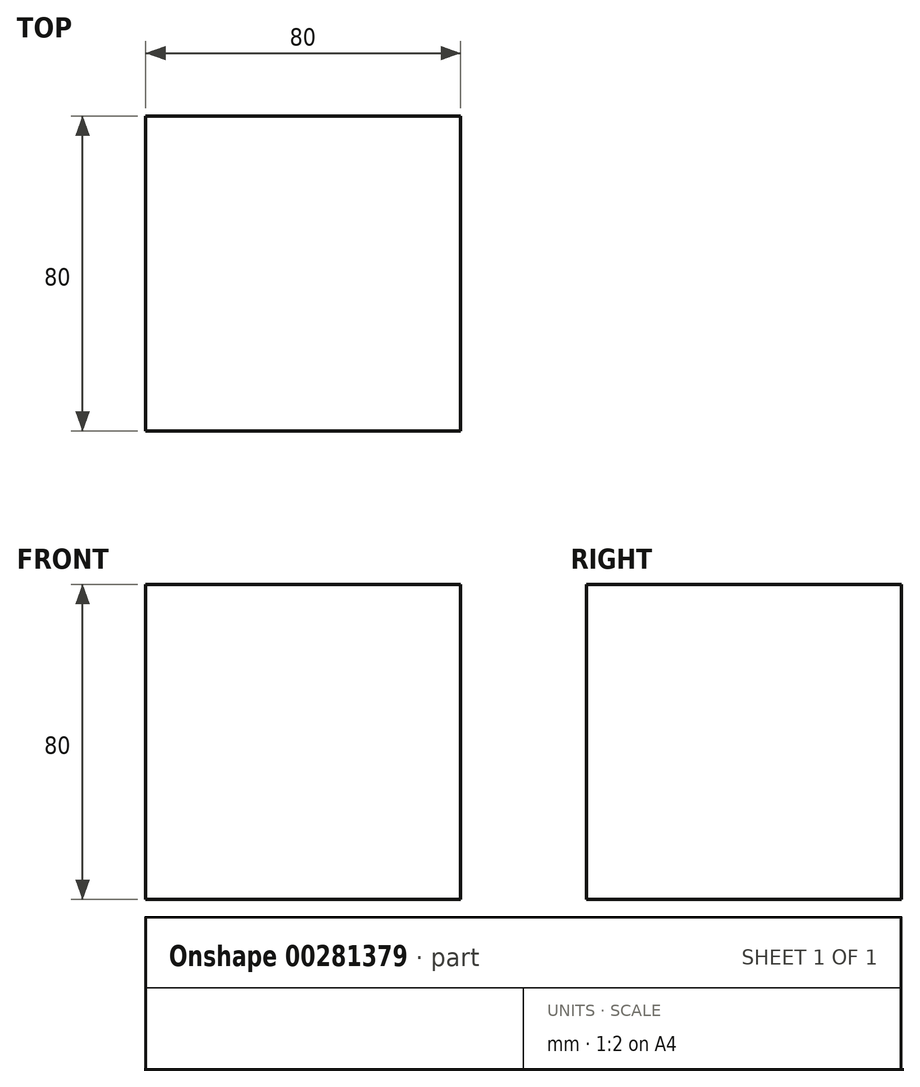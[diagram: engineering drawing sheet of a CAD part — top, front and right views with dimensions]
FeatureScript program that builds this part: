
annotation { "Feature Type Name" : "Feature", "Feature Type Description" : "" }
export const myFeature = defineFeature(function(context is Context, id is Id, definition is map)
    precondition{}
    {
        {
            var Q0;
            Q0=qCreatedBy(makeId("Front.planeOp"),FACE);
            var sketch = newSketch(context, id + "F0", { "sketchPlane" : qUnion([Q0])});
            skLineSegment(sketch, "E0.bottom", {"start": v(0, 0) * mm, "end": v(80, 0) * mm});
            skLineSegment(sketch, "E0.top", {"start": v(0, 80) * mm, "end": v(80, 80) * mm});
            skLineSegment(sketch, "E0.left", {"start": v(0, 0) * mm, "end": v(0, 80) * mm});
            skLineSegment(sketch, "E0.right", {"start": v(80, 0) * mm, "end": v(80, 80) * mm});
            skSolve(sketch);
        }
        {
            var Q0;
            Q0 = qSketchRegion(id + "F0", true);
            extrude(context, id + "F1", {"entities" : qUnion([Q0]), "depth" : 80 * mm});
        }
    });
